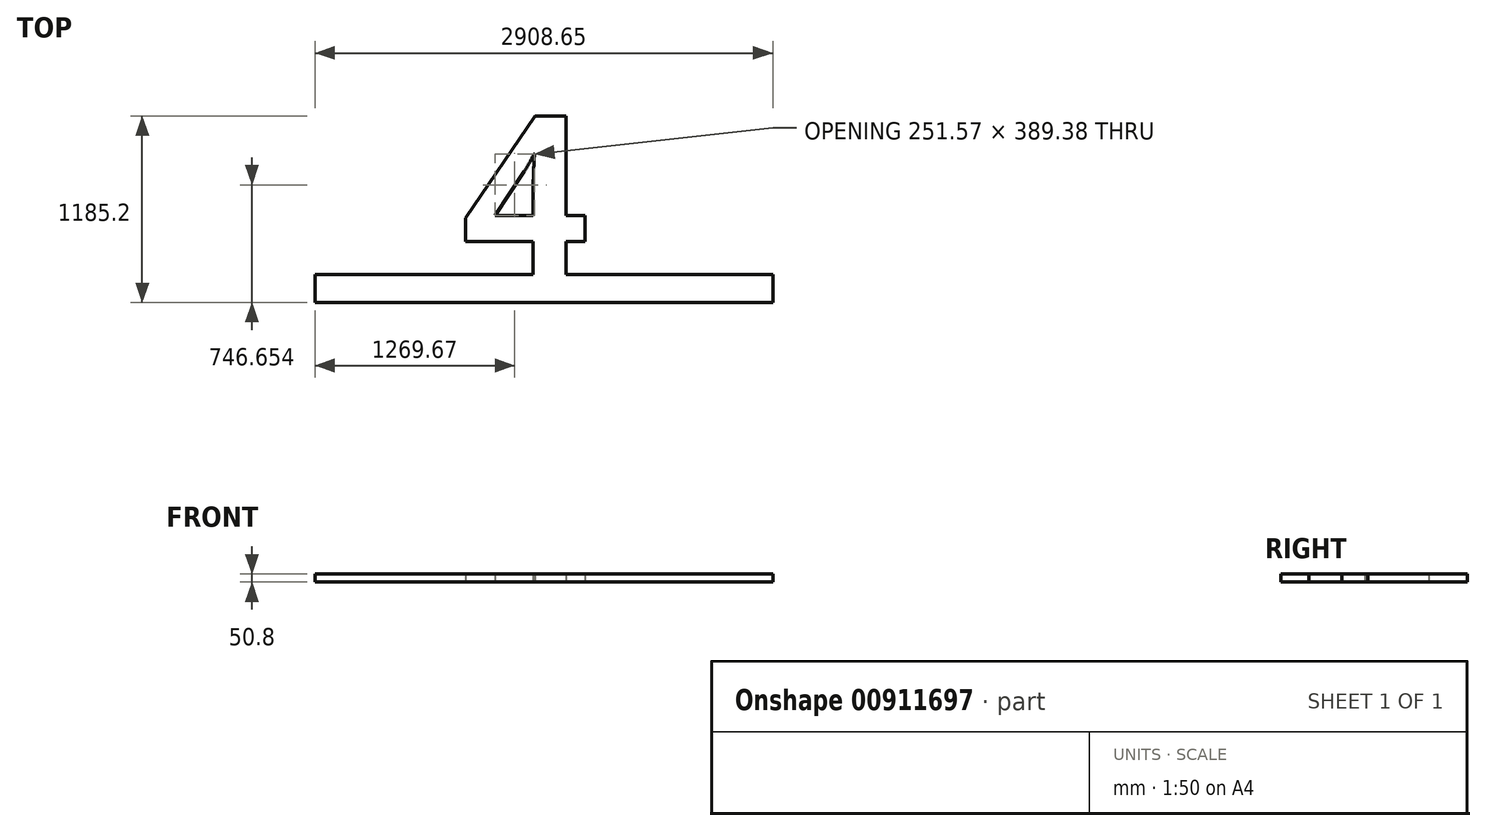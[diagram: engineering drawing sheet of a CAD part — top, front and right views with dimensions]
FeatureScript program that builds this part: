
annotation { "Feature Type Name" : "Feature", "Feature Type Description" : "" }
export const myFeature = defineFeature(function(context is Context, id is Id, definition is map)
    precondition{}
    {
        {
            var Q0;
            Q0=qCreatedBy(makeId("Top.planeOp"),FACE);
            var sketch = newSketch(context, id + "F0", { "sketchPlane" : qUnion([Q0])});
            skLineSegment(sketch, "E0.bottom", {"start": v(-281.19, -177.8) * mm, "end": v(2627.46, -177.8) * mm});
            skLineSegment(sketch, "E0.top", {"start": v(-281.19, 0) * mm, "end": v(2627.46, 0) * mm});
            skLineSegment(sketch, "E0.left", {"start": v(-281.19, -177.8) * mm, "end": v(-281.19, 0) * mm});
            skLineSegment(sketch, "E0.right", {"start": v(2627.46, -177.8) * mm, "end": v(2627.46, 0) * mm});
            skText(sketch, "E1", { "text": "14H", "fontName": "OpenSans-Bold.ttf"});
            const initialGuessF0  = {"E1": [-0.15419, 0, 1, 0, 1.016]};
            skSetInitialGuess(sketch, initialGuessF0);
            skSolve(sketch);
        }
        {
            var Q0;
            {var subQ0=sQuery(id+"F0.wireOp",EDGE,"d5d90416-0cdc-48ac-b64b-d5d0caaf983f.sketch_text.stroke-12");var subQ1=sQuery(id+"F0.wireOp",EDGE,"E0.top");var subQ2=makeQuery(id+"F0.imprint","INTERSECT",VERTEX,{"derivedFrom":[subQ1,subQ0]});Q0=makeQuery(id+"F0.imprint","IMPRINT",FACE,{"disambiguationData":[TD([[makeQuery(id+"F0.imprint","IMPRINT",EDGE,{"disambiguationData":[TD([[subQ2,-1.0]])],"derivedFrom":subQ1}),-1.0]])]});}
            var Q1;
            {var subQ6=sQuery(id+"F0.wireOp",EDGE,"d5d90416-0cdc-48ac-b64b-d5d0caaf983f.sketch_text.stroke-10");Q1=makeQuery(id+"F0.imprint","IMPRINT",FACE,{"disambiguationData":[TD([[makeQuery(id+"F0.imprint","IMPRINT",EDGE,{"derivedFrom":subQ6}),-1.0]])]});}
            var Q2;
            Q2=makeQuery(id+"F0.imprint","IMPRINT",FACE,{"disambiguationData":[TD([[makeQuery(id+"F0.imprint","IMPRINT",EDGE,{"derivedFrom":sQuery(id+"F0.wireOp",EDGE,"E0.bottom")}),1.0]])]});
            var Q3;
            Q3=makeQuery(id+"F0.imprint","IMPRINT",FACE,{"disambiguationData":[TD([[makeQuery(id+"F0.imprint","IMPRINT",EDGE,{"derivedFrom":sQuery(id+"F0.wireOp",EDGE,"d5d90416-0cdc-48ac-b64b-d5d0caaf983f.sketch_text.stroke-26")}),-1.0]])]});
            var Q4;
            Q4=makeQuery(id+"F0.imprint","IMPRINT",FACE,{"disambiguationData":[TD([[makeQuery(id+"F0.imprint","IMPRINT",EDGE,{"derivedFrom":sQuery(id+"F0.wireOp",EDGE,"d5d90416-0cdc-48ac-b64b-d5d0caaf983f.sketch_text.stroke-0")}),-1.0]])]});
            var Q5;
            Q5=makeQuery(id+"F0.imprint","IMPRINT",FACE,{"disambiguationData":[TD([[makeQuery(id+"F0.imprint","IMPRINT",EDGE,{"derivedFrom":sQuery(id+"F0.wireOp",EDGE,"eadfe806-04ac-4918-bb0a-3f37c2bbbc6a.sketch_text.stroke-10")}),-1.0]])]});
            var Q6;
            Q6=makeQuery(id+"F0.imprint","IMPRINT",FACE,{"disambiguationData":[TD([[makeQuery(id+"F0.imprint","IMPRINT",EDGE,{"derivedFrom":sQuery(id+"F0.wireOp",EDGE,"eadfe806-04ac-4918-bb0a-3f37c2bbbc6a.sketch_text.stroke-0")}),-1.0]])]});
            var Q7;
            Q7=makeQuery(id+"F0.imprint","IMPRINT",FACE,{"disambiguationData":[TD([[makeQuery(id+"F0.imprint","IMPRINT",EDGE,{"derivedFrom":sQuery(id+"F0.wireOp",EDGE,"eadfe806-04ac-4918-bb0a-3f37c2bbbc6a.sketch_text.stroke-20")}),-1.0]])]});
            var Q8;
            Q8=makeQuery(id+"F0.imprint","IMPRINT",FACE,{"disambiguationData":[TD([[makeQuery(id+"F0.imprint","IMPRINT",EDGE,{"derivedFrom":sQuery(id+"F0.wireOp",EDGE,"7b9dad4d-f56e-4f66-a96d-e45d99efa82c.sketch_text.stroke-0")}),-1.0]])]});
            var Q9;
            Q9=makeQuery(id+"F0.imprint","IMPRINT",FACE,{"disambiguationData":[TD([[makeQuery(id+"F0.imprint","IMPRINT",EDGE,{"derivedFrom":sQuery(id+"F0.wireOp",EDGE,"7b9dad4d-f56e-4f66-a96d-e45d99efa82c.sketch_text.stroke-10")}),-1.0]])]});
            var Q10;
            Q10=makeQuery(id+"F0.imprint","IMPRINT",FACE,{"disambiguationData":[TD([[makeQuery(id+"F0.imprint","IMPRINT",EDGE,{"derivedFrom":sQuery(id+"F0.wireOp",EDGE,"7b9dad4d-f56e-4f66-a96d-e45d99efa82c.sketch_text.stroke-34")}),-1.0]])]});
            var Q11;
            {var subQ0=sQuery(id+"F0.wireOp",EDGE,"dcbf4fd3-fc6b-438e-9322-ba9460cc3787.sketch_text.stroke-17");var subQ1=sQuery(id+"F0.wireOp",EDGE,"E0.top");var subQ2=makeQuery(id+"F0.imprint","INTERSECT",VERTEX,{"derivedFrom":[subQ1,subQ0]});Q11=makeQuery(id+"F0.imprint","IMPRINT",FACE,{"disambiguationData":[TD([[makeQuery(id+"F0.imprint","IMPRINT",EDGE,{"disambiguationData":[TD([[subQ2,-1.0]])],"derivedFrom":subQ1}),-1.0]])]});}
            var Q12;
            Q12=makeQuery(id+"F0.imprint","IMPRINT",FACE,{"disambiguationData":[TD([[makeQuery(id+"F0.imprint","IMPRINT",EDGE,{"derivedFrom":sQuery(id+"F0.wireOp",EDGE,"dcbf4fd3-fc6b-438e-9322-ba9460cc3787.sketch_text.stroke-10")}),-1.0]])]});
            var Q13;
            Q13=makeQuery(id+"F0.imprint","IMPRINT",FACE,{"disambiguationData":[TD([[makeQuery(id+"F0.imprint","IMPRINT",EDGE,{"derivedFrom":sQuery(id+"F0.wireOp",EDGE,"dcbf4fd3-fc6b-438e-9322-ba9460cc3787.sketch_text.stroke-37")}),-1.0]])]});
            var Q14;
            Q14=makeQuery(id+"F0.imprint","IMPRINT",FACE,{"disambiguationData":[TD([[makeQuery(id+"F0.imprint","IMPRINT",EDGE,{"derivedFrom":sQuery(id+"F0.wireOp",EDGE,"dcbf4fd3-fc6b-438e-9322-ba9460cc3787.sketch_text.stroke-0")}),-1.0]])]});
            var Q15;
            Q15=makeQuery(id+"F0.imprint","IMPRINT",FACE,{"disambiguationData":[TD([[makeQuery(id+"F0.imprint","IMPRINT",EDGE,{"derivedFrom":sQuery(id+"F0.wireOp",EDGE,"E1.sketch_text.stroke-10")}),-1.0]])]});
            var Q16;
            Q16=makeQuery(id+"F0.imprint","IMPRINT",FACE,{"disambiguationData":[TD([[makeQuery(id+"F0.imprint","IMPRINT",EDGE,{"derivedFrom":sQuery(id+"F0.wireOp",EDGE,"E1.sketch_text.stroke-28")}),-1.0]])]});
            var Q17;
            Q17=makeQuery(id+"F0.imprint","IMPRINT",FACE,{"disambiguationData":[TD([[makeQuery(id+"F0.imprint","IMPRINT",EDGE,{"derivedFrom":sQuery(id+"F0.wireOp",EDGE,"E1.sketch_text.stroke-0")}),-1.0]])]});
            extrude(context, id + "F1", {"entities" : qUnion([Q0, Q1, Q2, Q3, Q4, Q5, Q6, Q7, Q8, Q9, Q10, Q11, Q12, Q13, Q14, Q15, Q16, Q17]), "depth" : 50.8 * mm, "offsetDistance" : 25.4 * mm});
        }
    });
